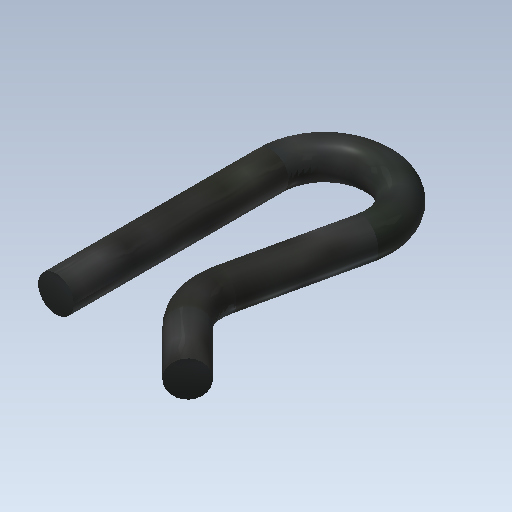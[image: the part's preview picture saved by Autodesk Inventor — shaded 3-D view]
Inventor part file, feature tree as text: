
AUTODESK INVENTOR PART (.ipt)
format: ipt  version: 2020 (Build 240168000, 168)  size: 148,480 bytes
history: native  units: mm
features: sketch x2, sweep x1
ambient origin geometry x8: Origin, YZ Plane, XZ Plane, XY Plane, X Axis, Y Axis, Z Axis, Center Point
bodies: Solid1 (feature_tree)
feature tree (3):
  sweep  "Sweep1"
  sketch  "Sketch1"  dims[d0=2.0mm d1=1.0mm]
  sketch  "Sketch2"  dims[d2=6.0mm d3=1.78mm d4=3.9mm d5=2.2mm d6=45.0deg d8=1.0mm d9=0.5mm d10=0.0mm d11=0.0mm]
